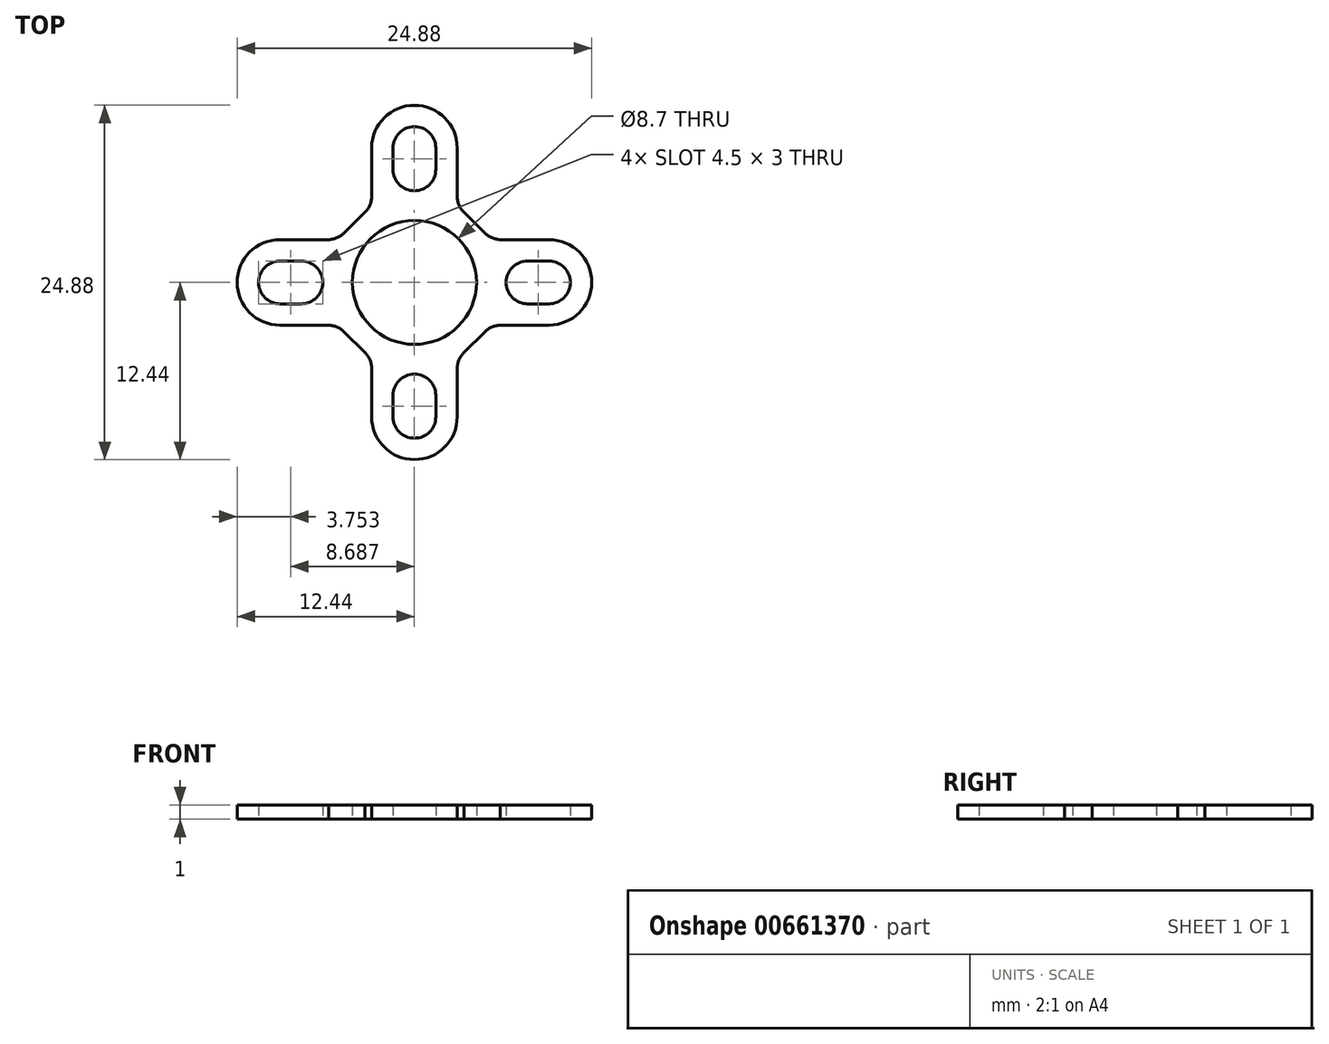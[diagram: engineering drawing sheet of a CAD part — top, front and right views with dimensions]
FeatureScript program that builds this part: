
annotation { "Feature Type Name" : "Feature", "Feature Type Description" : "" }
export const myFeature = defineFeature(function(context is Context, id is Id, definition is map)
    precondition{}
    {
        {
            var Q0;
            Q0=qCreatedBy(makeId("Top.planeOp"),FACE);
            var sketch = newSketch(context, id + "F0", { "sketchPlane" : qUnion([Q0])});
            skCircle(sketch, "E0", {"center": v(0, 0) * mm, "radius": 4.35 * mm});
            skLineSegment(sketch, "E1", {"start": v(0, 0) * mm, "end": v(3.08, 3.08) * mm, "construction": true});
            skLineSegment(sketch, "E2.MirrorCS", {"start": v(7.94, -1.5) * mm, "end": v(9.44, -1.5) * mm});
            skLineSegment(sketch, "E3.MirrorCS", {"start": v(7.94, 1.5) * mm, "end": v(9.44, 1.5) * mm});
            skArc(sketch, "E4.MirrorCS", {"start": v(9.44, -1.5) * mm, "mid": v(10.94, 0) * mm, "end": v(9.44, 1.5) * mm});
            skArc(sketch, "E5.MirrorCS", {"start": v(7.94, 1.5) * mm, "mid": v(6.44, 0) * mm, "end": v(7.94, -1.5) * mm});
            skArc(sketch, "E6.MirrorCS", {"start": v(-7.94, 1.5) * mm, "mid": v(-6.44, 0) * mm, "end": v(-7.94, -1.5) * mm});
            skPoint(sketch, "E7.visualSharp", {"position": v(4.69, -3.5) * mm});
            skPoint(sketch, "E8.visualSharp", {"position": v(-4.69, -3.5) * mm});
            skPoint(sketch, "E9.visualSharp", {"position": v(-5.43, -3.5) * mm});
            skLineSegment(sketch, "E10", {"start": v(-3.48, -4.93) * mm, "end": v(-4.93, -3.48) * mm});
            skPoint(sketch, "E11.visualSharp", {"position": v(-5.22, -3.19) * mm});
            skPoint(sketch, "E12.MirrorP", {"position": v(5.43, -3.5) * mm});
            skPoint(sketch, "E13.MirrorP", {"position": v(5.22, -3.19) * mm});
            skLineSegment(sketch, "E14.MirrorCS", {"start": v(3.48, -4.93) * mm, "end": v(4.93, -3.48) * mm});
            skPoint(sketch, "E15.MirrorP", {"position": v(-5.22, 3.19) * mm});
            skLineSegment(sketch, "E16.MirrorCS", {"start": v(-3.48, 4.93) * mm, "end": v(-4.93, 3.48) * mm});
            skPoint(sketch, "E17.MirrorP", {"position": v(-4.69, 3.5) * mm});
            skPoint(sketch, "E18.MirrorP", {"position": v(-5.43, 3.5) * mm});
            skPoint(sketch, "E19.MirrorP", {"position": v(-3.5, 5.53) * mm});
            skArc(sketch, "E20.MirrorC", {"start": v(3.08, 3.08) * mm, "mid": v(4.02, 1.66) * mm, "end": v(4.35, 0) * mm});
            skPoint(sketch, "E21.MirrorP", {"position": v(5.43, 3.5) * mm});
            skPoint(sketch, "E22.MirrorP", {"position": v(5.22, 3.19) * mm});
            skLineSegment(sketch, "E23.MirrorCS", {"start": v(3.48, 4.93) * mm, "end": v(4.93, 3.48) * mm});
            skPoint(sketch, "E24.MirrorP", {"position": v(4.69, 3.5) * mm});
            skLineSegment(sketch, "E25.MirrorCS", {"start": v(-9.44, -3) * mm, "end": v(-6.02, -3) * mm});
            skLineSegment(sketch, "E26.MirrorCS", {"start": v(-9.44, 3) * mm, "end": v(-6.02, 3) * mm});
            skArc(sketch, "E27.MirrorCS", {"start": v(-9.44, -1.5) * mm, "mid": v(-10.94, 0) * mm, "end": v(-9.44, 1.5) * mm});
            skLineSegment(sketch, "E28.MirrorCS", {"start": v(-7.94, -1.5) * mm, "end": v(-9.44, -1.5) * mm});
            skLineSegment(sketch, "E29.MirrorCS", {"start": v(-7.94, 1.5) * mm, "end": v(-9.44, 1.5) * mm});
            skArc(sketch, "E30", {"start": v(-9.44, -3) * mm, "mid": v(-12.44, 0) * mm, "end": v(-9.44, 3) * mm});
            skLineSegment(sketch, "E31.MirrorCS", {"start": v(9.44, 3) * mm, "end": v(6.02, 3) * mm});
            skLineSegment(sketch, "E32.MirrorCS", {"start": v(9.44, -3) * mm, "end": v(6.02, -3) * mm});
            skArc(sketch, "E33.MirrorCS", {"start": v(9.44, -3) * mm, "mid": v(12.44, 0) * mm, "end": v(9.44, 3) * mm});
            skLineSegment(sketch, "E34", {"start": v(0, 0) * mm, "end": v(-12.16, -12.16) * mm, "construction": true});
            skArc(sketch, "E35.MirrorCS", {"start": v(1.5, -7.94) * mm, "mid": v(0, -6.44) * mm, "end": v(-1.5, -7.94) * mm});
            skLineSegment(sketch, "E36.MirrorCS", {"start": v(-1.5, -7.94) * mm, "end": v(-1.5, -9.44) * mm});
            skLineSegment(sketch, "E37.MirrorCS", {"start": v(1.5, -7.94) * mm, "end": v(1.5, -9.44) * mm});
            skPoint(sketch, "E38.MirrorP", {"position": v(-3.5, -5.43) * mm});
            skPoint(sketch, "E39.MirrorP", {"position": v(3.5, -5.43) * mm});
            skLineSegment(sketch, "E40.MirrorCS", {"start": v(3, -9.44) * mm, "end": v(3, -6.02) * mm});
            skPoint(sketch, "E41.MirrorP", {"position": v(3.19, -5.22) * mm});
            skPoint(sketch, "E42.MirrorP", {"position": v(-3.19, -5.22) * mm});
            skArc(sketch, "E43.MirrorCS", {"start": v(-1.5, -9.44) * mm, "mid": v(0, -10.94) * mm, "end": v(1.5, -9.44) * mm});
            skLineSegment(sketch, "E44.MirrorCS", {"start": v(-3, -9.44) * mm, "end": v(-3, -6.02) * mm});
            skArc(sketch, "E45.MirrorCS", {"start": v(-3, -9.44) * mm, "mid": v(0, -12.44) * mm, "end": v(3, -9.44) * mm});
            skPoint(sketch, "E46.MirrorCS.end.orphan", {"position": v(-3, -6.02) * mm});
            skPoint(sketch, "E46.MirrorCS.start.orphan", {"position": v(-3.48, -4.93) * mm});
            skPoint(sketch, "E47.MirrorCS.start.orphan", {"position": v(3.5, -5.95) * mm});
            skLineSegment(sketch, "E48.MirrorCS", {"start": v(1.5, 7.94) * mm, "end": v(1.5, 9.44) * mm});
            skLineSegment(sketch, "E49.MirrorCS", {"start": v(-1.5, 7.94) * mm, "end": v(-1.5, 9.44) * mm});
            skArc(sketch, "E50.MirrorCS", {"start": v(1.5, 7.94) * mm, "mid": v(0, 6.44) * mm, "end": v(-1.5, 7.94) * mm});
            skPoint(sketch, "E51.MirrorP", {"position": v(-3.48, 4.93) * mm});
            skPoint(sketch, "E52.MirrorP", {"position": v(-3.5, 5.43) * mm});
            skLineSegment(sketch, "E53.MirrorCS", {"start": v(-3, 9.44) * mm, "end": v(-3, 6.02) * mm});
            skPoint(sketch, "E54.MirrorP", {"position": v(3.5, 5.43) * mm});
            skLineSegment(sketch, "E55.MirrorCS", {"start": v(3, 9.44) * mm, "end": v(3, 6.02) * mm});
            skArc(sketch, "E56.MirrorCS", {"start": v(-1.5, 9.44) * mm, "mid": v(0, 10.94) * mm, "end": v(1.5, 9.44) * mm});
            skPoint(sketch, "E57.MirrorCS.end.orphan", {"position": v(-6.02, 3) * mm});
            skPoint(sketch, "E11.filletArc.end.orphan", {"position": v(-6.02, -3) * mm});
            skPoint(sketch, "E58.filletArc.start.orphan", {"position": v(-3.5, -5.95) * mm});
            skPoint(sketch, "E59.MirrorCS.end.orphan", {"position": v(3, -6.02) * mm});
            skPoint(sketch, "E59.MirrorCS.start.orphan", {"position": v(3.48, -4.93) * mm});
            skPoint(sketch, "E60.MirrorCS.end.orphan", {"position": v(6.02, -3) * mm});
            skPoint(sketch, "E61.MirrorCS.end.orphan", {"position": v(6.02, 3) * mm});
            skArc(sketch, "E62", {"start": v(-4.93, 3.48) * mm, "mid": v(-5.43, 3.14) * mm, "end": v(-6.02, 3) * mm});
            skArc(sketch, "E63", {"start": v(-3, 6.02) * mm, "mid": v(-3.13, 5.42) * mm, "end": v(-3.48, 4.93) * mm});
            skArc(sketch, "E64", {"start": v(3, 6.02) * mm, "mid": v(3.13, 5.42) * mm, "end": v(3.48, 4.93) * mm});
            skArc(sketch, "E65", {"start": v(4.93, 3.48) * mm, "mid": v(5.43, 3.14) * mm, "end": v(6.02, 3) * mm});
            skArc(sketch, "E66", {"start": v(4.93, -3.48) * mm, "mid": v(5.43, -3.14) * mm, "end": v(6.02, -3) * mm});
            skArc(sketch, "E67", {"start": v(-4.93, -3.48) * mm, "mid": v(-5.43, -3.14) * mm, "end": v(-6.02, -3) * mm});
            skArc(sketch, "E68.MirrorCS", {"start": v(3, -6.02) * mm, "mid": v(3.13, -5.42) * mm, "end": v(3.48, -4.93) * mm});
            skArc(sketch, "E69.MirrorCS", {"start": v(-3, -6.02) * mm, "mid": v(-3.13, -5.42) * mm, "end": v(-3.48, -4.93) * mm});
            skArc(sketch, "E70", {"start": v(-3, 9.44) * mm, "mid": v(0, 12.44) * mm, "end": v(3, 9.44) * mm});
            skSolve(sketch);
        }
        {
            var Q0;
            Q0 = qSketchRegion(id + "F0", true);
            extrude(context, id + "F1", {"entities" : qUnion([Q0]), "depth" : 1 * mm, "offsetDistance" : 25 * mm});
        }
    });
